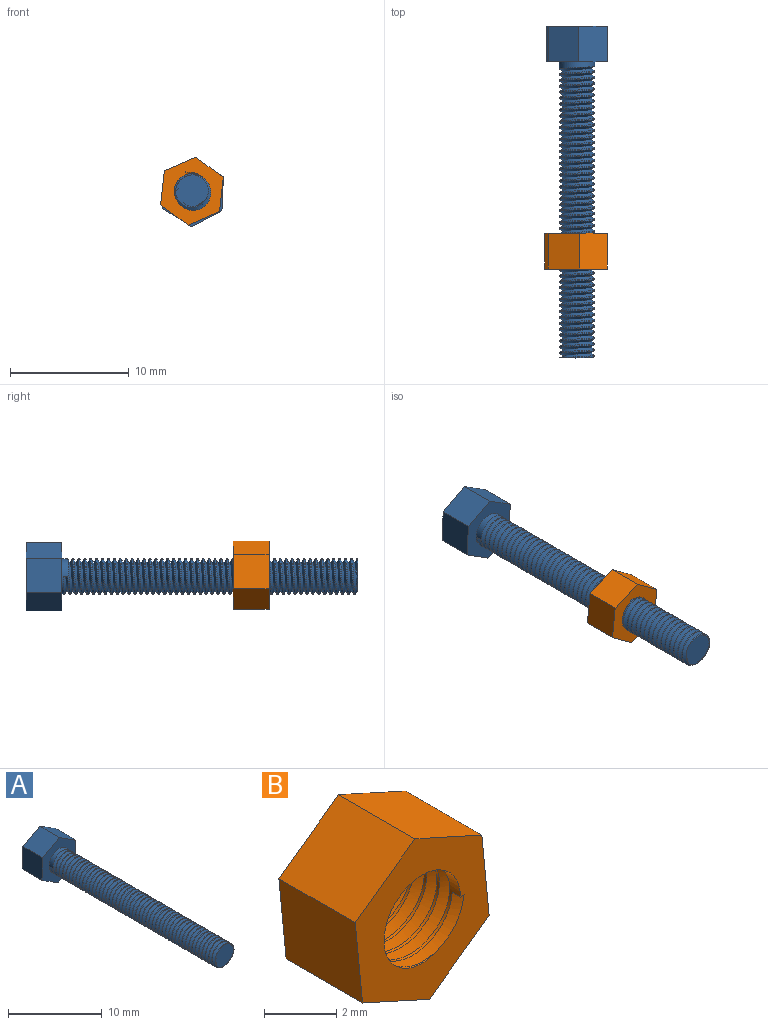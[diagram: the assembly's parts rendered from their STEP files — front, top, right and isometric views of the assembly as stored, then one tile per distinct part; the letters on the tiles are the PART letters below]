
ASSEMBLY  parts=2 mates=1
PART A: 62 faces, bbox 5.3x28.5x6 mm
  f0: cylinder r=1.5mm len=3mm, axis (0,1,0), area 4.2mm2, adj f1,f56,f59,f60,f61
  f1: cylinder r=1.5mm len=3mm, axis (0,1,0), area 0.9mm2, adj f0,f2,f60,f61
  f2: cylinder r=1.5mm len=3mm, axis (0,1,0), area 0.9mm2, adj f1,f3,f60,f61
  f3: cylinder r=1.5mm len=3mm, axis (0,1,0), area 0.9mm2, adj f2,f4,f60,f61
  f4: cylinder r=1.5mm len=3mm, axis (0,1,0), area 0.9mm2, adj f3,f5,f60,f61
  f5: cylinder r=1.5mm len=3mm, axis (0,1,0), area 0.9mm2, adj f4,f6,f60,f61
  f6: cylinder r=1.5mm len=3mm, axis (0,1,0), area 0.9mm2, adj f5,f7,f60,f61
  f7: cylinder r=1.5mm len=3mm, axis (0,1,0), area 0.9mm2, adj f6,f8,f60,f61
  f8: cylinder r=1.5mm len=3mm, axis (0,1,0), area 0.9mm2, adj f7,f9,f60,f61
  f9: cylinder r=1.5mm len=3mm, axis (0,1,0), area 0.9mm2, adj f8,f10,f60,f61
  f10: cylinder r=1.5mm len=3mm, axis (0,1,0), area 0.9mm2, adj f9,f11,f60,f61
  f11: cylinder r=1.5mm len=3mm, axis (0,1,0), area 0.9mm2, adj f10,f12,f60,f61
  f12: cylinder r=1.5mm len=3mm, axis (0,1,0), area 0.9mm2, adj f11,f13,f60,f61
  f13: cylinder r=1.5mm len=3mm, axis (0,1,0), area 0.9mm2, adj f12,f14,f60,f61
  f14: cylinder r=1.5mm len=3mm, axis (0,1,0), area 0.9mm2, adj f13,f15,f60,f61
  f15: cylinder r=1.5mm len=3mm, axis (0,1,0), area 0.9mm2, adj f14,f16,f60,f61
  f16: cylinder r=1.5mm len=3mm, axis (0,1,0), area 0.9mm2, adj f15,f17,f60,f61
  f17: cylinder r=1.5mm len=3mm, axis (0,1,0), area 0.9mm2, adj f16,f18,f60,f61
  f18: cylinder r=1.5mm len=3mm, axis (0,1,0), area 0.9mm2, adj f17,f19,f60,f61
  f19: cylinder r=1.5mm len=3mm, axis (0,1,0), area 0.9mm2, adj f18,f20,f60,f61
  f20: cylinder r=1.5mm len=3mm, axis (0,1,0), area 0.9mm2, adj f19,f21,f60,f61
  f21: cylinder r=1.5mm len=3mm, axis (0,1,0), area 0.9mm2, adj f20,f22,f60,f61
  f22: cylinder r=1.5mm len=3mm, axis (0,1,0), area 0.9mm2, adj f21,f23,f60,f61
  f23: cylinder r=1.5mm len=3mm, axis (0,1,0), area 0.9mm2, adj f22,f24,f60,f61
  f24: cylinder r=1.5mm len=3mm, axis (0,1,0), area 0.9mm2, adj f23,f25,f60,f61
  f25: cylinder r=1.5mm len=3mm, axis (0,1,0), area 0.9mm2, adj f24,f26,f60,f61
  f26: cylinder r=1.5mm len=3mm, axis (0,1,0), area 0.9mm2, adj f25,f27,f60,f61
  f27: cylinder r=1.5mm len=3mm, axis (0,1,0), area 0.9mm2, adj f26,f28,f60,f61
  f28: cylinder r=1.5mm len=3mm, axis (0,1,0), area 0.9mm2, adj f27,f29,f60,f61
  f29: cylinder r=1.5mm len=3mm, axis (0,1,0), area 0.9mm2, adj f28,f30,f60,f61
  f30: cylinder r=1.5mm len=3mm, axis (0,1,0), area 0.9mm2, adj f29,f31,f60,f61
  f31: cylinder r=1.5mm len=3mm, axis (0,1,0), area 0.9mm2, adj f30,f32,f60,f61
  f32: cylinder r=1.5mm len=3mm, axis (0,1,0), area 0.9mm2, adj f31,f33,f60,f61
  f33: cylinder r=1.5mm len=3mm, axis (0,1,0), area 0.9mm2, adj f32,f34,f60,f61
  f34: cylinder r=1.5mm len=3mm, axis (0,1,0), area 0.9mm2, adj f33,f35,f60,f61
  f35: cylinder r=1.5mm len=3mm, axis (0,1,0), area 0.9mm2, adj f34,f36,f60,f61
  f36: cylinder r=1.5mm len=3mm, axis (0,1,0), area 0.9mm2, adj f35,f37,f60,f61
  f37: cylinder r=1.5mm len=3mm, axis (0,1,0), area 0.9mm2, adj f36,f38,f60,f61
  f38: cylinder r=1.5mm len=3mm, axis (0,1,0), area 0.9mm2, adj f37,f39,f60,f61
  f39: cylinder r=1.5mm len=3mm, axis (0,1,0), area 0.9mm2, adj f38,f40,f60,f61
  f40: cylinder r=1.5mm len=3mm, axis (0,1,0), area 0.9mm2, adj f39,f41,f60,f61
  f41: cylinder r=1.5mm len=3mm, axis (0,1,0), area 0.9mm2, adj f40,f42,f60,f61
  f42: cylinder r=1.5mm len=3mm, axis (0,1,0), area 0.9mm2, adj f41,f43,f60,f61
  f43: cylinder r=1.5mm len=3mm, axis (0,1,0), area 0.9mm2, adj f42,f44,f60,f61
  f44: cylinder r=1.5mm len=3mm, axis (0,1,0), area 0.9mm2, adj f43,f45,f60,f61
  f45: cylinder r=1.5mm len=3mm, axis (0,1,0), area 0.9mm2, adj f44,f46,f60,f61
  f46: cylinder r=1.5mm len=3mm, axis (0,1,0), area 0.9mm2, adj f45,f47,f60,f61
  f47: cylinder r=1.5mm len=3mm, axis (0,1,0), area 0.9mm2, adj f46,f48,f60,f61
  f48: cylinder r=1.5mm len=3mm, axis (0,1,0), area 0.9mm2, adj f47,f49,f60,f61
  f49: cylinder r=1.5mm len=1.42mm, axis (0,1,0), area 0.1mm2, adj f48,f58,f61
  f50: plane 3x2.44mm, normal (0.54,0,0.84), area 8.7mm2, adj f51,f55,f56,f57
  f51: plane 3x2.56mm, normal (-0.46,0,0.89), area 8.7mm2, adj f50,f52,f56,f57
  f52: plane 3x2.88mm, normal (-1,0,0.04), area 8.7mm2, adj f51,f53,f56,f57
  f53: plane 3x2.44mm, normal (-0.54,0,-0.84), area 8.7mm2, adj f52,f54,f56,f57
  f54: plane 3x2.56mm, normal (0.46,0,-0.89), area 8.7mm2, adj f53,f55,f56,f57
  f55: plane 3x2.88mm, normal (1,0,-0.04), area 8.7mm2, adj f50,f54,f56,f57
  f56: plane 5.77x5.12mm, normal (0,-1,0), area 14.6mm2, adj f0,f50,f51,f52,f53,f54,f55
  f57: plane 5.77x5.12mm, normal (0,1,0), area 21.7mm2, adj f50,f51,f52,f53,f54,f55
  f58: plane 2.98x2.98mm, normal (0,-1,0), area 5.9mm2, adj f49,f60,f61
  f59: plane 0.4x0.35mm, normal (0,0,-1), area 0.1mm2, adj f0,f60,f61
  f60: bspline ~25.12x3.46mm, area 165.5mm2, adj f0,f1,f2,f3,f4,f5,f6,f7
  f61: bspline ~24.95x3.46mm, area 163.9mm2, adj f0,f1,f2,f3,f4,f5,f6,f7
PART B: 13 faces, bbox 5.5x3.5x6 mm
  f0: plane 3x2.63mm, normal (0.41,0,0.91), area 8.7mm2, adj f1,f5,f6,f7
  f1: plane 3x2.35mm, normal (-0.58,0,0.81), area 8.7mm2, adj f0,f2,f6,f7
  f2: plane 3x2.87mm, normal (-1,0,-0.1), area 8.7mm2, adj f1,f3,f6,f7
  f3: plane 3x2.63mm, normal (-0.41,0,-0.91), area 8.7mm2, adj f2,f4,f6,f7
  f4: plane 3x2.35mm, normal (0.58,0,-0.81), area 8.7mm2, adj f3,f5,f6,f7
  f5: plane 3x2.87mm, normal (1,0,0.1), area 8.7mm2, adj f0,f4,f6,f7
  f6: plane 5.77x5.29mm, normal (0,-1,0), area 14.5mm2, adj f0,f1,f2,f3,f4,f5,f8,f10
  f7: plane 5.97x5.49mm, normal (0,1,0), area 13.3mm2, adj f0,f1,f2,f3,f4,f5,f8,f9
  f8: cylinder r=1.5mm len=3mm, axis (0,-1,0), area 6.6mm2, adj f6,f7,f9,f10,f11,f12
  f9: plane 0.13x0.08mm, normal (0,0,1), area 0mm2, adj f7,f8,f10
  f10: bspline ~4.26x3.69mm, area 24.8mm2, adj f6,f7,f8,f9,f11,f12
  f11: bspline ~4.26x3.69mm, area 23.4mm2, adj f7,f8,f10,f12
  f12: plane 0.35x0.33mm, normal (0,0,-1), area 0.1mm2, adj f6,f8,f10,f11
PLACE A t=(-14.67,9.62,-13.01)mm
PLACE B rot(axis=(0,-1,0),108deg) t=(-14.77,-7.88,-12.89)mm
MATE cylindrical A.f58 <-> B.f8  axis (0,-1,0) through (-14.77,-18.38,-12.89)mm
